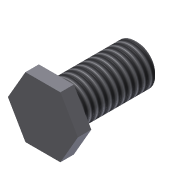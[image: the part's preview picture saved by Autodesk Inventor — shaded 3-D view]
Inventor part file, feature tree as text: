
AUTODESK INVENTOR PART (.ipt)
format: ipt  version: 2011 (Build 150239000, 239)  size: 96,768 bytes
history: native  units: in
note: dims shown in document units (in); Inventor stores cm internally (conversion verified against a paired STEP export)
features: extrude x2, sketch x2, thread x1, chamfer x1
ambient origin geometry x8: Origin, YZ Plane, XZ Plane, XY Plane, X Axis, Y Axis, Z Axis, Center Point
bodies: Solid1 (feature_tree)
feature tree (6):
  extrude  "Extrusion1"  Depth=0.75in TaperAngle=0.0deg
  extrude  "Extrusion2"  Depth=0.125in TaperAngle=0.0deg
  thread  "Thread1"  [1 undecoded]
  chamfer  "Chamfer1"  Distance=0.02in Angle=45.0deg
  sketch  "Sketch1"  dims[d0=0.375in d1=0.75in d2=0.0in]
  sketch  "Sketch2"  dims[d3=0.5625in d4=0.125in d5=0.0in d6=1.0in d7=0.0in d8=0.02in d9=0.125in d10=45.0deg]
note: 1 required parameter value undecoded (feature->parameter linkage not recoverable at this tier; creation-order binding heuristic only, values carry confidence <= 0.55)
